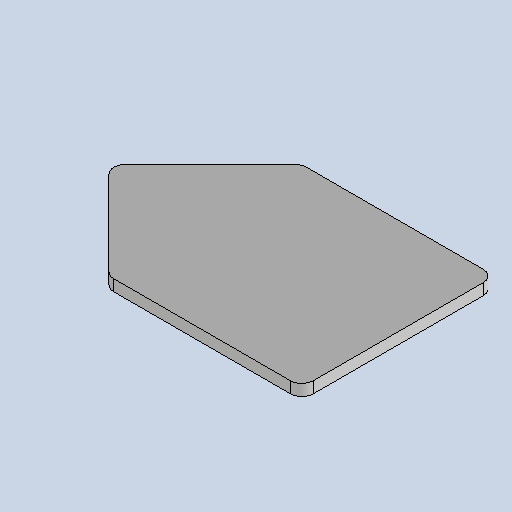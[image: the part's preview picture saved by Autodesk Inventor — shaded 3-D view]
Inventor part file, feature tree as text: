
AUTODESK INVENTOR PART (.ipt)
format: ipt  version: 2025.3 (Build 293356030, 356C)  size: 183,296 bytes
history: native  units: mm
features: other x2, sheet_metal_op x1, chamfer x1, sketch x1
ambient origin geometry x8: Origin, YZ Plane, XZ Plane, XY Plane, X Axis, Y Axis, Z Axis, Center Point
bodies: Body1 (feature_tree)
feature tree (5):
  sheet_metal_op  "Face3"
  chamfer  "Corner Round1"
  sketch  "Sketch1"  dims[d154=34.0mm d155=34.0mm d156=2.0mm d178=2.0mm d180=17.0mm]
  other  "Plate5"
  other  "Definition1"
